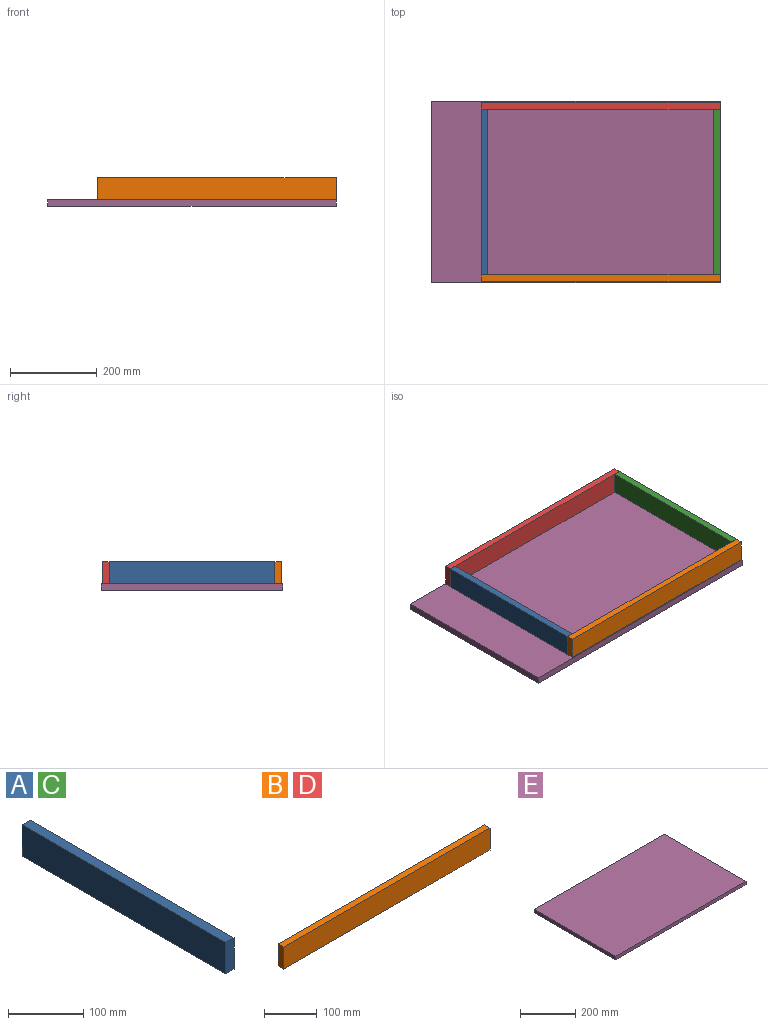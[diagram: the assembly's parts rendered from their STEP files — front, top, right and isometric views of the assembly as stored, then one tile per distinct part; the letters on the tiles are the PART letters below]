
ASSEMBLY  parts=5 mates=4
PART A: 6 faces, bbox 15.1x382.6x50.8 mm
  f0: plane 50.8x15.09mm, normal (0,1,0), area 766.5mm2, adj f1,f3,f4,f5
  f1: plane 382.57x15.09mm, normal (0,0,1), area 5772.1mm2, adj f0,f2,f4,f5
  f2: plane 50.8x15.09mm, normal (0,-1,0), area 766.5mm2, adj f1,f3,f4,f5
  f3: plane 382.57x15.09mm, normal (0,0,-1), area 5772.1mm2, adj f0,f2,f4,f5
  f4: plane 382.57x50.8mm, normal (1,0,0), area 19434.8mm2, adj f0,f1,f2,f3
  f5: plane 382.57x50.8mm, normal (-1,0,0), area 19434.8mm2, adj f0,f1,f2,f3
PART B: 6 faces, bbox 551.1x15.1x50.8 mm
  f0: plane 551.08x15.09mm, normal (0,0,1), area 8314.5mm2, adj f1,f3,f4,f5
  f1: plane 50.8x15.09mm, normal (-1,0,0), area 766.5mm2, adj f0,f2,f4,f5
  f2: plane 551.08x15.09mm, normal (0,0,-1), area 8314.5mm2, adj f1,f3,f4,f5
  f3: plane 50.8x15.09mm, normal (1,0,0), area 766.5mm2, adj f0,f2,f4,f5
  f4: plane 551.08x50.8mm, normal (0,-1,0), area 27994.8mm2, adj f0,f1,f2,f3
  f5: plane 551.08x50.8mm, normal (0,1,0), area 27994.8mm2, adj f0,f1,f2,f3
PART C: same geometry as A
PART D: same geometry as B
PART E: 6 faces, bbox 665.2x417.7x15.1 mm
  f0: plane 665.18x15.09mm, normal (0,1,0), area 10035.9mm2, adj f1,f3,f4,f5
  f1: plane 417.73x15.09mm, normal (-1,0,0), area 6302.5mm2, adj f0,f2,f4,f5
  f2: plane 665.18x15.09mm, normal (0,-1,0), area 10035.9mm2, adj f1,f3,f4,f5
  f3: plane 417.73x15.09mm, normal (1,0,0), area 6302.5mm2, adj f0,f2,f4,f5
  f4: plane 665.18x417.73mm, normal (0,0,1), area 277862.6mm2, adj f0,f1,f2,f3
  f5: plane 665.18x417.73mm, normal (0,0,-1), area 277862.6mm2, adj f0,f1,f2,f3
PLACE A t=(-283.46,-10.39,177.01)mm
PLACE B t=(12.77,-146.47,104.34)mm
PLACE C t=(252.53,-10.39,177.01)mm
PLACE D t=(12.77,251.19,104.34)mm
PLACE E t=(-116.59,0,2.49)mm
MATE fastened D.f4 <-> A.f0  axis (0,-1,0) through (-283.46,236.1,42.98)mm
MATE fastened D.f4 <-> C.f0  axis (0,-1,0) through (267.61,236.1,42.98)mm
MATE fastened C.f3 <-> E.f4  axis (0,0,-1) through (267.61,44.82,17.58)mm
MATE fastened C.f2 <-> B.f5  axis (0,-1,0) through (267.61,-146.47,42.98)mm
